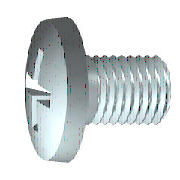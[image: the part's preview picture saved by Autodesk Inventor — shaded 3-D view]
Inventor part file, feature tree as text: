
AUTODESK INVENTOR PART (.ipt)
format: ipt  version: 2025.1 (Build 291241020, 241B)  size: 249,856 bytes
history: native  units: mm (DEFAULTED — no unit token found)
features: other x5, chamfer x4, fillet x1, pattern_circular x1
ambient origin geometry x8: Origin, YZ Plane, XZ Plane, XY Plane, X Axis, Y Axis, Z Axis, Center Point
bodies: Solid1 (feature_tree)
feature tree (11):
  chamfer  "Chanfrar1"  Distance=1.8mm
  chamfer  "Chanfrar2"  Distance=0.872665mm
  fillet  "Raio de arredondamento1"  [1 undecoded]
  pattern_circular  "Matriz polar1"  [2 undecoded]
  chamfer  "Chanfrar3"  Distance=0.1mm
  chamfer  "Chanfrar4"  Distance=0.2mm
  other  "MSC_A1"
  other  "MSC_PF1"
  other  "MSC_PT1"
  other  "Rascunho2"
  other  "Rascunho3"
note: 3 required parameter values undecoded (feature->parameter linkage not recoverable at this tier; creation-order binding heuristic only, values carry confidence <= 0.55)
